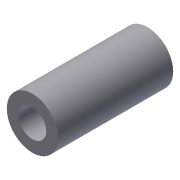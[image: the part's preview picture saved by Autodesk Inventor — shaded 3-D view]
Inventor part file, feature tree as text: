
AUTODESK INVENTOR PART (.ipt)
format: ipt  version: 2013 (Build 170138000, 138)  size: 89,600 bytes
history: native  units: in
note: dims shown in document units (in); Inventor stores cm internally (conversion verified against a paired STEP export)
features: extrude x1, sketch x1
ambient origin geometry x8: Origin, YZ Plane, XZ Plane, XY Plane, X Axis, Y Axis, Z Axis, Center Point
bodies: Solid1 (feature_tree)
feature tree (2):
  extrude  "Extrusion1"  Depth=0.5in
  sketch  "Sketch1"  dims[d0=0.27in d1=0.5in d2=1.125in d3=0.0in]
